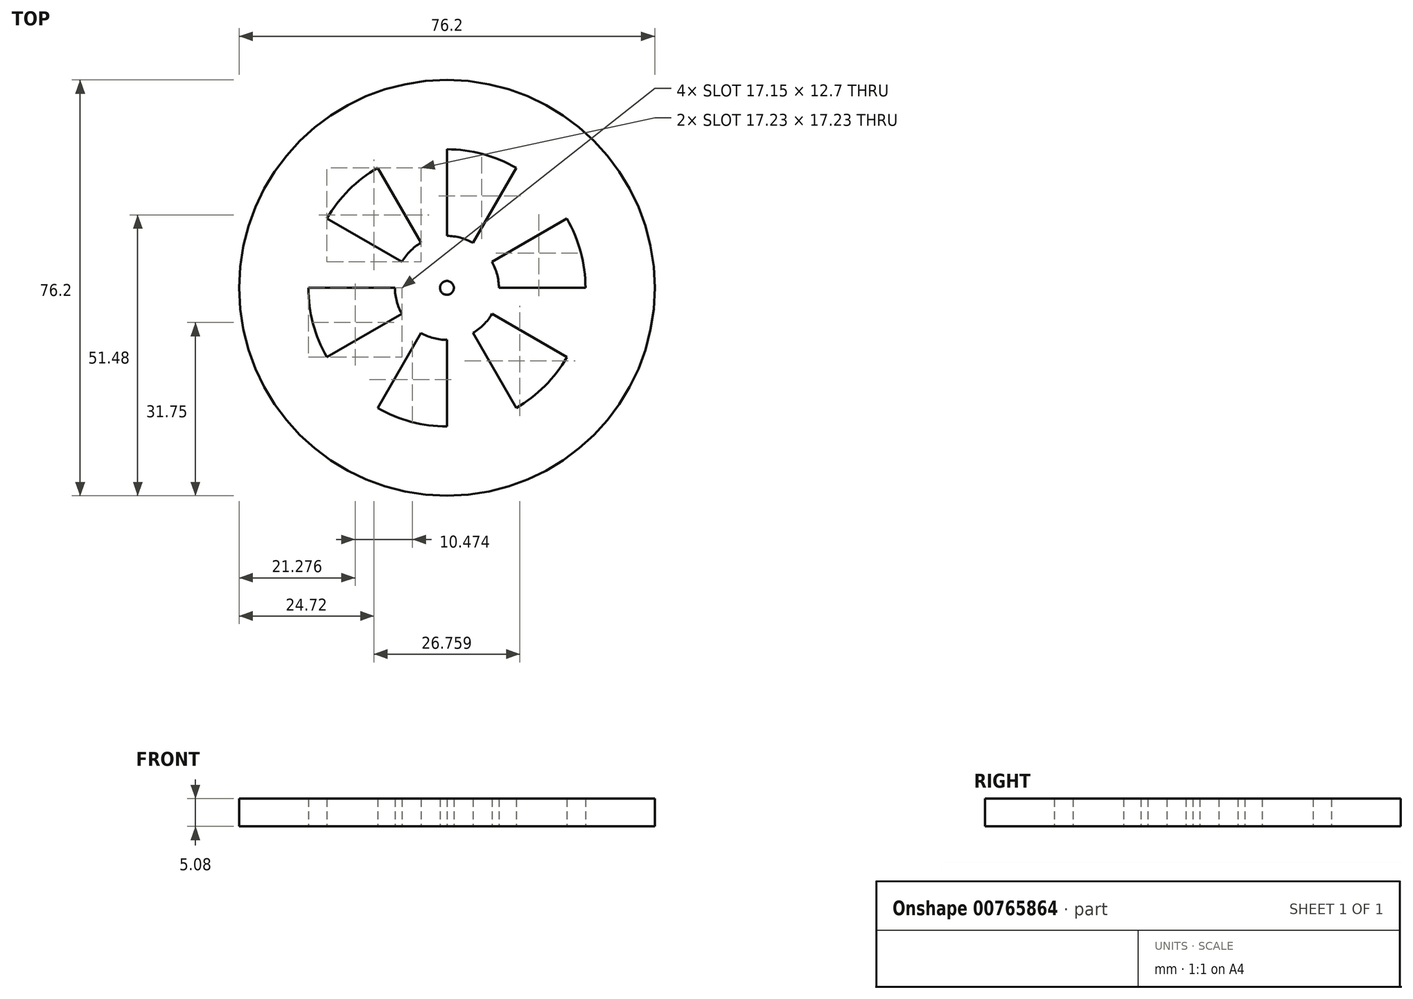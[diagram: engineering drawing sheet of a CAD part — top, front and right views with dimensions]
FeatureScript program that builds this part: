
annotation { "Feature Type Name" : "Feature", "Feature Type Description" : "" }
export const myFeature = defineFeature(function(context is Context, id is Id, definition is map)
    precondition{}
    {
        {
            var Q0;
            Q0=qCreatedBy(makeId("Top.planeOp"),FACE);
            var sketch = newSketch(context, id + "F0", { "sketchPlane" : qUnion([Q0])});
            skCircle(sketch, "E0", {"center": v(0, 0) * mm, "radius": 38.1 * mm});
            skCircle(sketch, "E1", {"center": v(0, 0) * mm, "radius": 25.4 * mm});
            skLineSegment(sketch, "E2", {"start": v(0, 0) * mm, "end": v(25.4, 0) * mm});
            skLineSegment(sketch, "E3", {"start": v(0, 0) * mm, "end": v(22, 12.7) * mm});
            skLineSegment(sketch, "E4", {"start": v(0, 0) * mm, "end": v(12.7, 22) * mm});
            skLineSegment(sketch, "E5", {"start": v(0, 0) * mm, "end": v(0, 25.4) * mm});
            skLineSegment(sketch, "E6", {"start": v(0, 0) * mm, "end": v(-12.7, 22) * mm});
            skLineSegment(sketch, "E7", {"start": v(0, 0) * mm, "end": v(-22, 12.7) * mm});
            skLineSegment(sketch, "E8", {"start": v(0, 0) * mm, "end": v(-25.4, 0) * mm});
            skLineSegment(sketch, "E9", {"start": v(0, 0) * mm, "end": v(-22, -12.7) * mm});
            skLineSegment(sketch, "E10", {"start": v(0, 0) * mm, "end": v(-12.7, -22) * mm});
            skLineSegment(sketch, "E11", {"start": v(0, 0) * mm, "end": v(0, -25.4) * mm});
            skLineSegment(sketch, "E12", {"start": v(0, 0) * mm, "end": v(12.7, -22) * mm});
            skLineSegment(sketch, "E13", {"start": v(0, 0) * mm, "end": v(22, -12.7) * mm});
            skCircle(sketch, "E14", {"center": v(0, 0) * mm, "radius": 9.53 * mm});
            skCircle(sketch, "E15", {"center": v(0, 0) * mm, "radius": 1.27 * mm});
            skSolve(sketch);
        }
        {
            var Q0;
            {var subQ0=sQuery(id+"F0.wireOp",EDGE,"E15");var subQ1=sQuery(id+"F0.wireOp",EDGE,"E9");var subQ2=makeQuery(id+"F0.imprint","INTERSECT",VERTEX,{"derivedFrom":[subQ1,subQ0]});Q0=makeQuery(id+"F0.imprint","IMPRINT",FACE,{"disambiguationData":[TD([[makeQuery(id+"F0.imprint","IMPRINT",EDGE,{"disambiguationData":[TD([[subQ2,-1.0]])],"derivedFrom":subQ1}),1.0]])]});}
            var Q1;
            {var subQ0=sQuery(id+"F0.wireOp",EDGE,"E15");var subQ1=sQuery(id+"F0.wireOp",EDGE,"E10");var subQ2=makeQuery(id+"F0.imprint","INTERSECT",VERTEX,{"derivedFrom":[subQ1,subQ0]});Q1=makeQuery(id+"F0.imprint","IMPRINT",FACE,{"disambiguationData":[TD([[makeQuery(id+"F0.imprint","IMPRINT",EDGE,{"disambiguationData":[TD([[subQ2,-1.0]])],"derivedFrom":subQ1}),1.0]])]});}
            var Q2;
            {var subQ0=sQuery(id+"F0.wireOp",EDGE,"E15");var subQ1=sQuery(id+"F0.wireOp",EDGE,"E11");var subQ2=makeQuery(id+"F0.imprint","INTERSECT",VERTEX,{"derivedFrom":[subQ1,subQ0]});Q2=makeQuery(id+"F0.imprint","IMPRINT",FACE,{"disambiguationData":[TD([[makeQuery(id+"F0.imprint","IMPRINT",EDGE,{"disambiguationData":[TD([[subQ2,-1.0]])],"derivedFrom":subQ1}),1.0]])]});}
            var Q3;
            {var subQ0=sQuery(id+"F0.wireOp",EDGE,"E15");var subQ1=sQuery(id+"F0.wireOp",EDGE,"E12");var subQ2=makeQuery(id+"F0.imprint","INTERSECT",VERTEX,{"derivedFrom":[subQ1,subQ0]});Q3=makeQuery(id+"F0.imprint","IMPRINT",FACE,{"disambiguationData":[TD([[makeQuery(id+"F0.imprint","IMPRINT",EDGE,{"disambiguationData":[TD([[subQ2,-1.0]])],"derivedFrom":subQ1}),1.0]])]});}
            var Q4;
            {var subQ0=sQuery(id+"F0.wireOp",EDGE,"E15");var subQ1=sQuery(id+"F0.wireOp",EDGE,"E2");var subQ2=makeQuery(id+"F0.imprint","INTERSECT",VERTEX,{"derivedFrom":[subQ1,subQ0]});Q4=makeQuery(id+"F0.imprint","IMPRINT",FACE,{"disambiguationData":[TD([[makeQuery(id+"F0.imprint","IMPRINT",EDGE,{"disambiguationData":[TD([[subQ2,-1.0]])],"derivedFrom":subQ1}),-1.0]])]});}
            var Q5;
            {var subQ0=sQuery(id+"F0.wireOp",EDGE,"E15");var subQ1=sQuery(id+"F0.wireOp",EDGE,"E2");var subQ2=makeQuery(id+"F0.imprint","INTERSECT",VERTEX,{"derivedFrom":[subQ1,subQ0]});Q5=makeQuery(id+"F0.imprint","IMPRINT",FACE,{"disambiguationData":[TD([[makeQuery(id+"F0.imprint","IMPRINT",EDGE,{"disambiguationData":[TD([[subQ2,-1.0]])],"derivedFrom":subQ1}),1.0]])]});}
            var Q6;
            {var subQ0=sQuery(id+"F0.wireOp",EDGE,"E15");var subQ1=sQuery(id+"F0.wireOp",EDGE,"E3");var subQ2=makeQuery(id+"F0.imprint","INTERSECT",VERTEX,{"derivedFrom":[subQ1,subQ0]});Q6=makeQuery(id+"F0.imprint","IMPRINT",FACE,{"disambiguationData":[TD([[makeQuery(id+"F0.imprint","IMPRINT",EDGE,{"disambiguationData":[TD([[subQ2,-1.0]])],"derivedFrom":subQ1}),1.0]])]});}
            var Q7;
            {var subQ0=sQuery(id+"F0.wireOp",EDGE,"E15");var subQ1=sQuery(id+"F0.wireOp",EDGE,"E4");var subQ2=makeQuery(id+"F0.imprint","INTERSECT",VERTEX,{"derivedFrom":[subQ1,subQ0]});Q7=makeQuery(id+"F0.imprint","IMPRINT",FACE,{"disambiguationData":[TD([[makeQuery(id+"F0.imprint","IMPRINT",EDGE,{"disambiguationData":[TD([[subQ2,-1.0]])],"derivedFrom":subQ1}),1.0]])]});}
            var Q8;
            {var subQ0=sQuery(id+"F0.wireOp",EDGE,"E15");var subQ1=sQuery(id+"F0.wireOp",EDGE,"E5");var subQ2=makeQuery(id+"F0.imprint","INTERSECT",VERTEX,{"derivedFrom":[subQ1,subQ0]});Q8=makeQuery(id+"F0.imprint","IMPRINT",FACE,{"disambiguationData":[TD([[makeQuery(id+"F0.imprint","IMPRINT",EDGE,{"disambiguationData":[TD([[subQ2,-1.0]])],"derivedFrom":subQ1}),1.0]])]});}
            var Q9;
            {var subQ0=sQuery(id+"F0.wireOp",EDGE,"E15");var subQ1=sQuery(id+"F0.wireOp",EDGE,"E6");var subQ2=makeQuery(id+"F0.imprint","INTERSECT",VERTEX,{"derivedFrom":[subQ1,subQ0]});Q9=makeQuery(id+"F0.imprint","IMPRINT",FACE,{"disambiguationData":[TD([[makeQuery(id+"F0.imprint","IMPRINT",EDGE,{"disambiguationData":[TD([[subQ2,-1.0]])],"derivedFrom":subQ1}),1.0]])]});}
            var Q10;
            {var subQ0=sQuery(id+"F0.wireOp",EDGE,"E15");var subQ1=sQuery(id+"F0.wireOp",EDGE,"E7");var subQ2=makeQuery(id+"F0.imprint","INTERSECT",VERTEX,{"derivedFrom":[subQ1,subQ0]});Q10=makeQuery(id+"F0.imprint","IMPRINT",FACE,{"disambiguationData":[TD([[makeQuery(id+"F0.imprint","IMPRINT",EDGE,{"disambiguationData":[TD([[subQ2,-1.0]])],"derivedFrom":subQ1}),1.0]])]});}
            var Q11;
            {var subQ0=sQuery(id+"F0.wireOp",EDGE,"E15");var subQ1=sQuery(id+"F0.wireOp",EDGE,"E8");var subQ2=makeQuery(id+"F0.imprint","INTERSECT",VERTEX,{"derivedFrom":[subQ1,subQ0]});Q11=makeQuery(id+"F0.imprint","IMPRINT",FACE,{"disambiguationData":[TD([[makeQuery(id+"F0.imprint","IMPRINT",EDGE,{"disambiguationData":[TD([[subQ2,-1.0]])],"derivedFrom":subQ1}),1.0]])]});}
            var Q12;
            {var subQ0=sQuery(id+"F0.wireOp",EDGE,"E3");var subQ1=sQuery(id+"F0.wireOp",EDGE,"E1");var subQ2=makeQuery(id+"F0.imprint","INTERSECT",VERTEX,{"derivedFrom":[subQ1,subQ0]});Q12=makeQuery(id+"F0.imprint","IMPRINT",FACE,{"disambiguationData":[TD([[makeQuery(id+"F0.imprint","IMPRINT",EDGE,{"disambiguationData":[TD([[subQ2,-1.0]])],"derivedFrom":subQ1}),1.0]])]});}
            var Q13;
            {var subQ0=sQuery(id+"F0.wireOp",EDGE,"E7");var subQ1=sQuery(id+"F0.wireOp",EDGE,"E1");var subQ2=makeQuery(id+"F0.imprint","INTERSECT",VERTEX,{"derivedFrom":[subQ1,subQ0]});Q13=makeQuery(id+"F0.imprint","IMPRINT",FACE,{"disambiguationData":[TD([[makeQuery(id+"F0.imprint","IMPRINT",EDGE,{"disambiguationData":[TD([[subQ2,-1.0]])],"derivedFrom":subQ1}),1.0]])]});}
            var Q14;
            {var subQ0=sQuery(id+"F0.wireOp",EDGE,"E9");var subQ1=sQuery(id+"F0.wireOp",EDGE,"E1");var subQ2=makeQuery(id+"F0.imprint","INTERSECT",VERTEX,{"derivedFrom":[subQ1,subQ0]});Q14=makeQuery(id+"F0.imprint","IMPRINT",FACE,{"disambiguationData":[TD([[makeQuery(id+"F0.imprint","IMPRINT",EDGE,{"disambiguationData":[TD([[subQ2,-1.0]])],"derivedFrom":subQ1}),1.0]])]});}
            var Q15;
            {var subQ0=sQuery(id+"F0.wireOp",EDGE,"E5");var subQ1=sQuery(id+"F0.wireOp",EDGE,"E1");var subQ2=makeQuery(id+"F0.imprint","INTERSECT",VERTEX,{"derivedFrom":[subQ1,subQ0]});Q15=makeQuery(id+"F0.imprint","IMPRINT",FACE,{"disambiguationData":[TD([[makeQuery(id+"F0.imprint","IMPRINT",EDGE,{"disambiguationData":[TD([[subQ2,-1.0]])],"derivedFrom":subQ1}),1.0]])]});}
            var Q16;
            {var subQ0=sQuery(id+"F0.wireOp",EDGE,"E11");var subQ1=sQuery(id+"F0.wireOp",EDGE,"E1");var subQ2=makeQuery(id+"F0.imprint","INTERSECT",VERTEX,{"derivedFrom":[subQ1,subQ0]});Q16=makeQuery(id+"F0.imprint","IMPRINT",FACE,{"disambiguationData":[TD([[makeQuery(id+"F0.imprint","IMPRINT",EDGE,{"disambiguationData":[TD([[subQ2,-1.0]])],"derivedFrom":subQ1}),1.0]])]});}
            var Q17;
            {var subQ0=sQuery(id+"F0.wireOp",EDGE,"E2");var subQ1=sQuery(id+"F0.wireOp",EDGE,"E1");var subQ2=makeQuery(id+"F0.imprint","INTERSECT",VERTEX,{"derivedFrom":[subQ1,subQ0]});Q17=makeQuery(id+"F0.imprint","IMPRINT",FACE,{"disambiguationData":[TD([[makeQuery(id+"F0.imprint","IMPRINT",EDGE,{"disambiguationData":[TD([[subQ2,1.0]])],"derivedFrom":subQ1}),1.0]])]});}
            var Q18;
            Q18=makeQuery(id+"F0.imprint","IMPRINT",FACE,{"disambiguationData":[TD([[makeQuery(id+"F0.imprint","IMPRINT",EDGE,{"derivedFrom":sQuery(id+"F0.wireOp",EDGE,"E0")}),1.0]])]});
            extrude(context, id + "F1", {"entities" : qUnion([Q0, Q1, Q2, Q3, Q4, Q5, Q6, Q7, Q8, Q9, Q10, Q11, Q12, Q13, Q14, Q15, Q16, Q17, Q18]), "depth" : 5.08 * mm, "offsetDistance" : 25.4 * mm});
        }
    });
